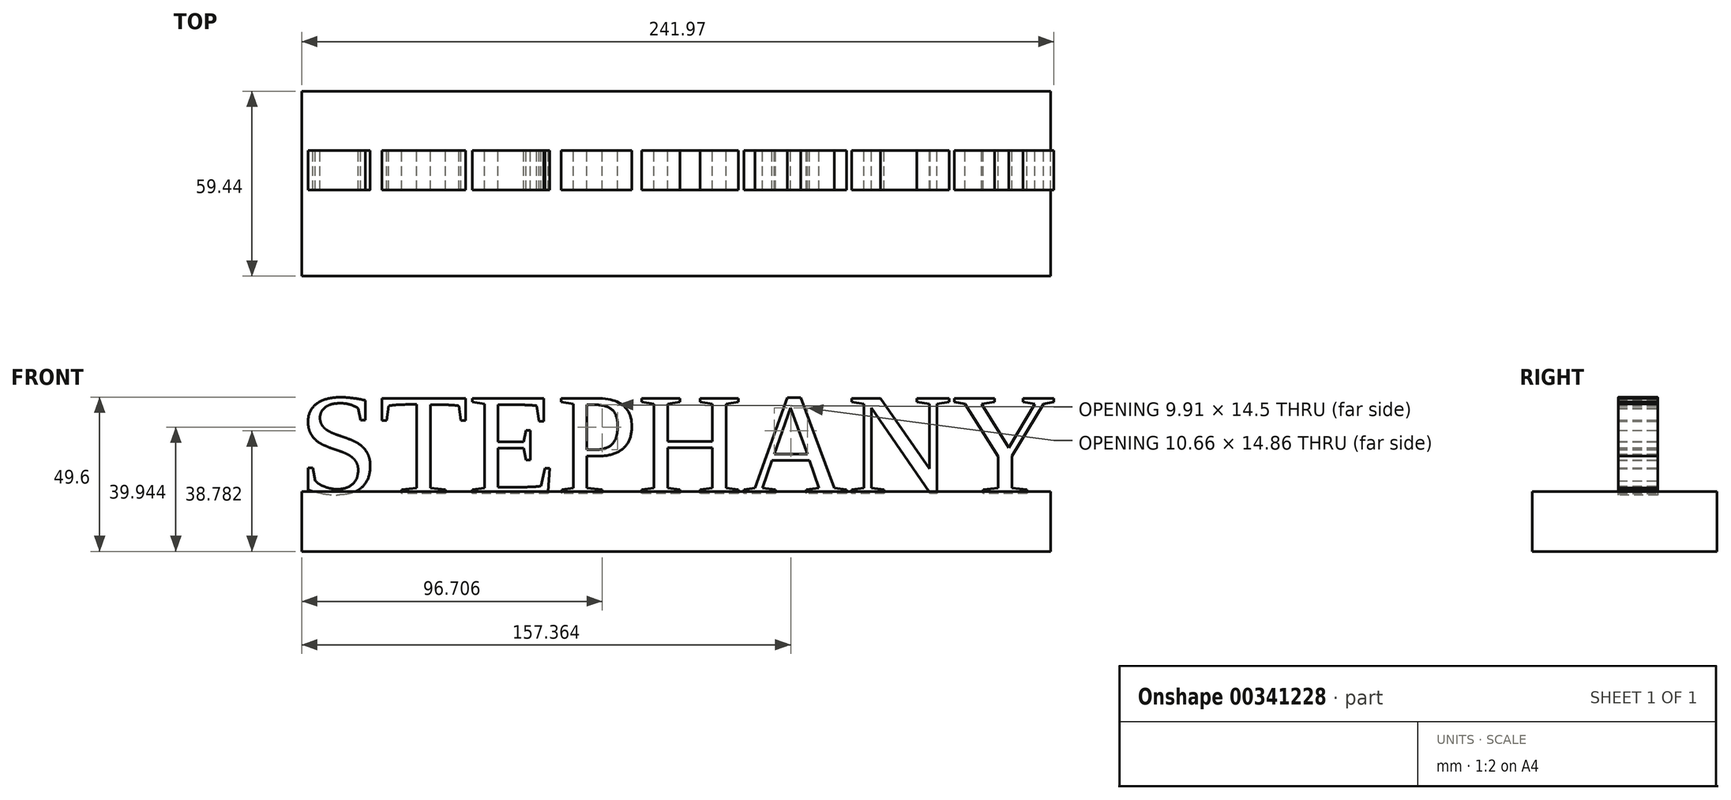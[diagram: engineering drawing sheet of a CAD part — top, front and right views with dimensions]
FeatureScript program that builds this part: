
annotation { "Feature Type Name" : "Feature", "Feature Type Description" : "" }
export const myFeature = defineFeature(function(context is Context, id is Id, definition is map)
    precondition{}
    {
        {
            var Q0;
            Q0=qCreatedBy(makeId("Front.planeOp"),FACE);
            var sketch = newSketch(context, id + "F0", { "sketchPlane" : qUnion([Q0])});
            skText(sketch, "E0", { "text": "STEPHANY", "fontName": "Tinos-Regular.ttf"});
            const initialGuessF0  = {"E0": [-0.1249, -0.0144, 1, 0, 0.03367]};
            skSetInitialGuess(sketch, initialGuessF0);
            skSolve(sketch);
        }
        {
            var Q0;
            Q0 = qSketchRegion(id + "F0", true);
            extrude(context, id + "F1", {"entities" : qUnion([Q0]), "depth" : 12.7 * mm});
        }
        {
            var Q0;
            Q0=qCreatedBy(makeId("Front.planeOp"),FACE);
            var sketch = newSketch(context, id + "F2", { "sketchPlane" : qUnion([Q0])});
            skLineSegment(sketch, "E1.bottom", {"start": v(-123.84, -13.81) * mm, "end": v(117.05, -13.81) * mm});
            skLineSegment(sketch, "E1.top", {"start": v(-123.84, -33.03) * mm, "end": v(117.05, -33.03) * mm});
            skLineSegment(sketch, "E1.left", {"start": v(-123.84, -13.81) * mm, "end": v(-123.84, -33.03) * mm});
            skLineSegment(sketch, "E1.right", {"start": v(117.05, -13.81) * mm, "end": v(117.05, -33.03) * mm});
            skSolve(sketch);
        }
        {
            var Q0;
            Q0=makeQuery(id+"F2.imprint","IMPRINT",FACE,{"disambiguationData":[TD([[makeQuery(id+"F2.imprint","IMPRINT",EDGE,{"derivedFrom":sQuery(id+"F2.wireOp",EDGE,"E1.bottom")}),-1.0]])]});
            extrude(context, id + "F3", {"entities" : qUnion([Q0]), "depth" : 40.4 * mm, "hasSecondDirection" : true, "secondDirectionOppositeDirection" : true, "secondDirectionDepth" : 19.05 * mm});
        }
    });
